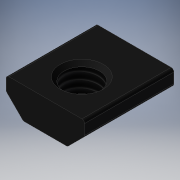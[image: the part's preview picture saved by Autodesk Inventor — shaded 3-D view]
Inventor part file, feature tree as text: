
AUTODESK INVENTOR PART (.ipt)
format: ipt  version: 2025 (Build 290162000, 162)  size: 145,920 bytes
history: native  units: mm
features: other x7, sketch x2, extrude x1, revolve x1, thread x1
ambient origin geometry x8: Origin, YZ Plane, XZ Plane, XY Plane, X Axis, Y Axis, Z Axis, Center Point
bodies: Solid1 (feature_tree)
feature tree (12):
  extrude  "Extrusion1"  TaperAngle=360.0deg  [1 undecoded]
  revolve  "Revolution1"  [1 undecoded]
  thread  "Thread1"  [1 undecoded]
  other  "tnut_XY"
  other  "tnut_YZ"
  other  "tnut_ZX"
  other  "tnut_X"
  other  "tnut_Y"
  other  "tnut_Z"
  other  "tnut_Center"
  sketch  "Sketch_1"  dims[d0=12.446mm d1=0.0mm d2=360.0deg]
  sketch  "Sketch_4"  dims[d3=3.2604mm d4=0.0mm d5=0.0mm]
note: 3 required parameter values undecoded (feature->parameter linkage not recoverable at this tier; creation-order binding heuristic only, values carry confidence <= 0.55)